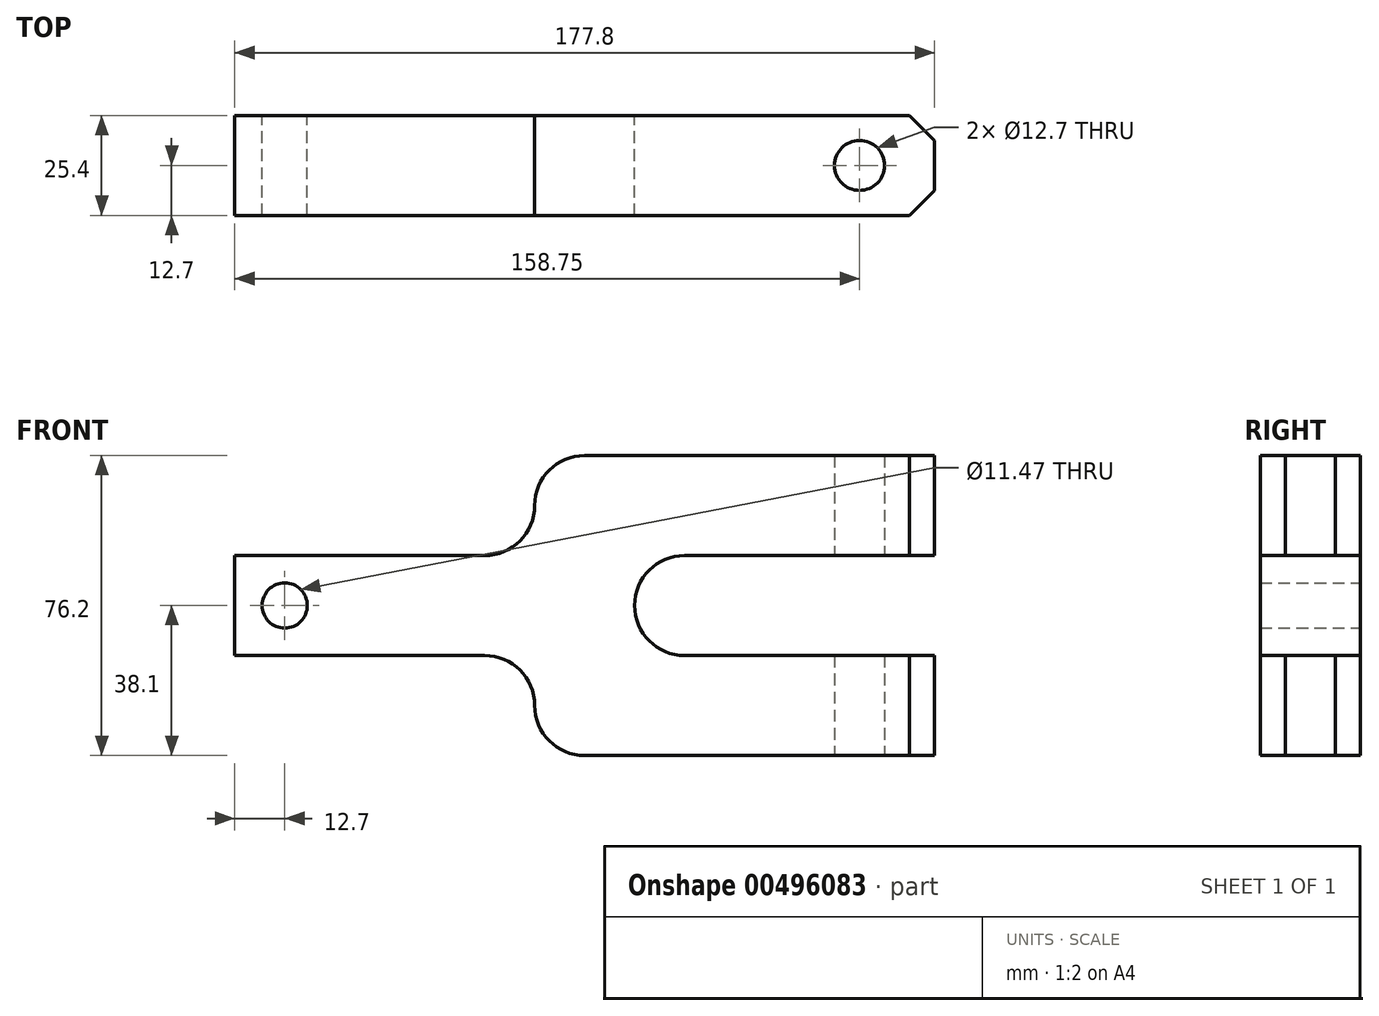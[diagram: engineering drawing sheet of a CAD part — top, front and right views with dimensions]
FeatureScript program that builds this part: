
annotation { "Feature Type Name" : "Feature", "Feature Type Description" : "" }
export const myFeature = defineFeature(function(context is Context, id is Id, definition is map)
    precondition{}
    {
        {
            var Q0;
            Q0=qCreatedBy(makeId("Front.planeOp"),FACE);
            var sketch = newSketch(context, id + "F0", { "sketchPlane" : qUnion([Q0])});
            skLineSegment(sketch, "E0.bottom", {"start": v(26.9, 12.7) * mm, "end": v(-74.7, 12.7) * mm});
            skLineSegment(sketch, "E0.top", {"start": v(26.9, -12.7) * mm, "end": v(-74.7, -12.7) * mm});
            skLineSegment(sketch, "E0.left", {"start": v(26.9, 12.7) * mm, "end": v(26.9, -12.7) * mm});
            skLineSegment(sketch, "E0.right", {"start": v(-74.7, 12.7) * mm, "end": v(-74.7, -12.7) * mm});
            skPoint(sketch, "E0.middle", {"position": v(-23.9, 0) * mm});
            skLineSegment(sketch, "E1.bottom", {"start": v(1.5, 12.7) * mm, "end": v(103.1, 12.7) * mm});
            skLineSegment(sketch, "E1.top", {"start": v(1.5, 38.1) * mm, "end": v(103.1, 38.1) * mm});
            skLineSegment(sketch, "E1.left", {"start": v(1.5, 12.7) * mm, "end": v(1.5, 38.1) * mm});
            skLineSegment(sketch, "E1.right", {"start": v(103.1, 12.7) * mm, "end": v(103.1, 38.1) * mm});
            skPoint(sketch, "E1.middle", {"position": v(52.3, 25.4) * mm});
            skLineSegment(sketch, "E2.bottom", {"start": v(1.5, -12.7) * mm, "end": v(103.1, -12.7) * mm});
            skLineSegment(sketch, "E2.top", {"start": v(1.5, -38.1) * mm, "end": v(103.1, -38.1) * mm});
            skLineSegment(sketch, "E2.left", {"start": v(1.5, -12.7) * mm, "end": v(1.5, -38.1) * mm});
            skLineSegment(sketch, "E2.right", {"start": v(103.1, -12.7) * mm, "end": v(103.1, -38.1) * mm});
            skPoint(sketch, "E2.middle", {"position": v(52.3, -25.4) * mm});
            skCircle(sketch, "E3", {"center": v(-62, 0) * mm, "radius": 5.74 * mm});
            skSolve(sketch);
        }
        {
            var Q0;
            Q0 = qSketchRegion(id + "F0", true);
            extrude(context, id + "F1", {"entities" : qUnion([Q0]), "endBound" : BoundingType.SYMMETRIC, "depth" : 25.4 * mm});
        }
        {
            var Q0;
            Q0=makeQuery(id+"F1.opExtrude","SWEPT_EDGE",EDGE,{"disambiguationData":[OSD([sQuery(id+"F0.wireOp",EDGE,"E1.top"),sQuery(id+"F0.wireOp",EDGE,"E1.left")])]});
            var Q1;
            Q1=makeQuery(id+"F1.opExtrude","SWEPT_EDGE",EDGE,{"disambiguationData":[OSD([sQuery(id+"F0.wireOp",EDGE,"E0.bottom"),sQuery(id+"F0.wireOp",EDGE,"E1.bottom"),sQuery(id+"F0.wireOp",EDGE,"E1.left")])]});
            fillet(context, id + "F2", {"entities" : qUnion([Q0, Q1]), "radius" : 12.7 * mm, "tangentPropagation" : true, "allowEdgeOverflow" : false});
        }
        {
            var Q0;
            Q0=makeQuery(id+"F1.opExtrude","SWEPT_EDGE",EDGE,{"disambiguationData":[OSD([sQuery(id+"F0.wireOp",EDGE,"E0.left"),sQuery(id+"F0.wireOp",EDGE,"E1.bottom")])]});
            var Q1;
            Q1=makeQuery(id+"F1.opExtrude","SWEPT_EDGE",EDGE,{"disambiguationData":[OSD([sQuery(id+"F0.wireOp",EDGE,"E0.left"),sQuery(id+"F0.wireOp",EDGE,"E2.bottom")])]});
            fillet(context, id + "F3", {"entities" : qUnion([Q0, Q1]), "radius" : 12.7 * mm, "tangentPropagation" : true, "allowEdgeOverflow" : false});
        }
        {
            var Q0;
            Q0=makeQuery(id+"F1.opExtrude","SWEPT_EDGE",EDGE,{"disambiguationData":[OSD([sQuery(id+"F0.wireOp",EDGE,"E0.top"),sQuery(id+"F0.wireOp",EDGE,"E2.bottom"),sQuery(id+"F0.wireOp",EDGE,"E2.left")])]});
            var Q1;
            Q1=makeQuery(id+"F1.opExtrude","SWEPT_EDGE",EDGE,{"disambiguationData":[OSD([sQuery(id+"F0.wireOp",EDGE,"E2.top"),sQuery(id+"F0.wireOp",EDGE,"E2.left")])]});
            fillet(context, id + "F4", {"entities" : qUnion([Q0, Q1]), "radius" : 12.7 * mm, "tangentPropagation" : true, "allowEdgeOverflow" : false});
        }
        {
            var Q0;
            Q0=makeQuery(id+"F1.opExtrude","CAP_EDGE",EDGE,{"disambiguationData":[OSD([sQuery(id+"F0.wireOp",EDGE,"E1.right")])],"isStart":false});
            var Q1;
            Q1=makeQuery(id+"F1.opExtrude","CAP_EDGE",EDGE,{"disambiguationData":[OSD([sQuery(id+"F0.wireOp",EDGE,"E1.right")])],"isStart":true});
            chamfer(context, id + "F5", {"entities" : qUnion([Q0, Q1]), "chamferType" : ChamferType.OFFSET_ANGLE, "width" : 6.35 * mm, "oppositeDirection" : false, "angle" : 45 * degree, "tangentPropagation" : true});
        }
        {
            var Q0;
            Q0=makeQuery(id+"F1.opExtrude","CAP_EDGE",EDGE,{"disambiguationData":[OSD([sQuery(id+"F0.wireOp",EDGE,"E2.right")])],"isStart":false});
            var Q1;
            Q1=makeQuery(id+"F1.opExtrude","CAP_EDGE",EDGE,{"disambiguationData":[OSD([sQuery(id+"F0.wireOp",EDGE,"E2.right")])],"isStart":true});
            chamfer(context, id + "F6", {"entities" : qUnion([Q0, Q1]), "chamferType" : ChamferType.OFFSET_ANGLE, "width" : 6.35 * mm, "oppositeDirection" : false, "angle" : 45 * degree, "tangentPropagation" : true});
        }
        {
            var Q0;
            Q0=qCreatedBy(makeId("Top.planeOp"),FACE);
            var sketch = newSketch(context, id + "F7", { "sketchPlane" : qUnion([Q0])});
            skCircle(sketch, "E4", {"center": v(84.04, 0) * mm, "radius": 6.35 * mm});
            skSolve(sketch);
        }
        {
            var Q0;
            Q0 = qSketchRegion(id + "F7", true);
            extrude(context, id + "F8", {"entities" : qUnion([Q0]), "operationType" : NewBodyOperationType.REMOVE, "endBound" : BoundingType.SYMMETRIC, "depth" : 254 * mm});
        }
    });
